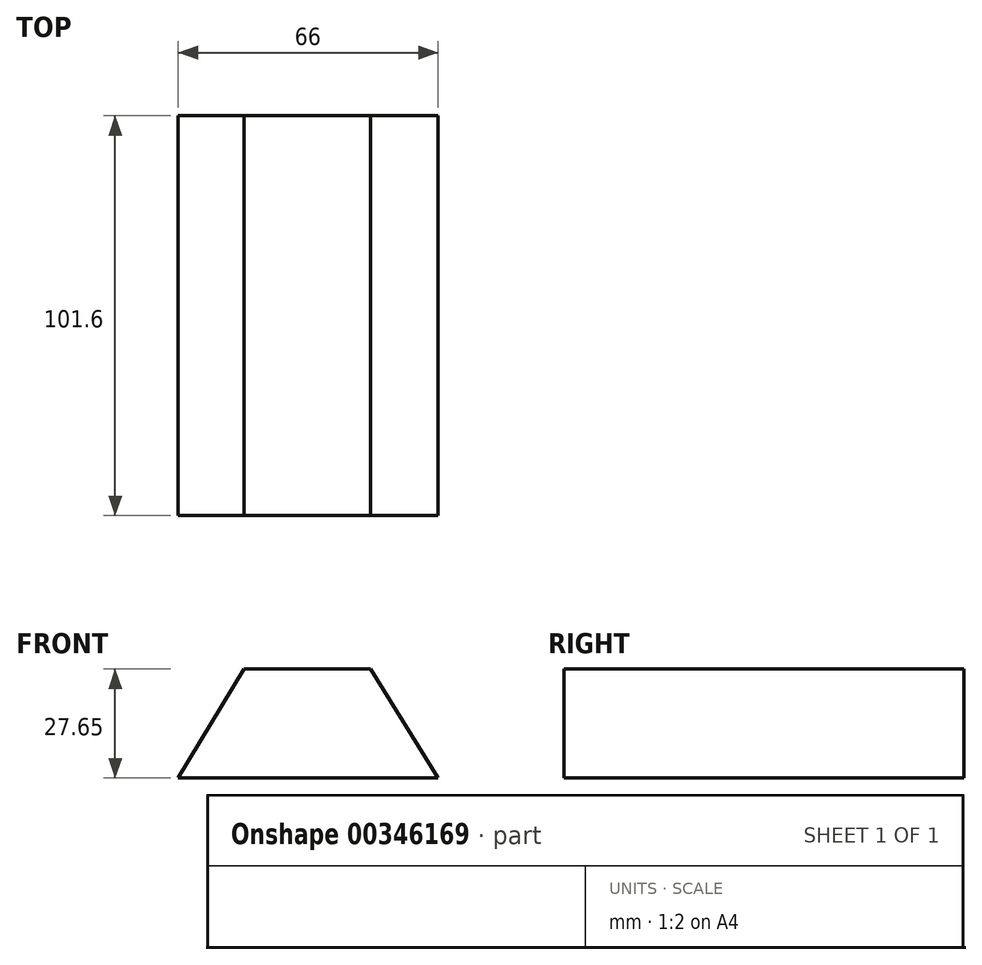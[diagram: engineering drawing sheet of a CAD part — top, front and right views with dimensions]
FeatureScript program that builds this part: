
annotation { "Feature Type Name" : "Feature", "Feature Type Description" : "" }
export const myFeature = defineFeature(function(context is Context, id is Id, definition is map)
    precondition{}
    {
        {
            var Q0;
            Q0=qCreatedBy(makeId("Front.planeOp"),FACE);
            var sketch = newSketch(context, id + "F0", { "sketchPlane" : qUnion([Q0])});
            skLineSegment(sketch, "E0", {"start": v(0, 0) * mm, "end": v(16.78, 27.65) * mm});
            skLineSegment(sketch, "E1", {"start": v(16.78, 27.65) * mm, "end": v(48.85, 27.65) * mm});
            skLineSegment(sketch, "E2", {"start": v(48.85, 27.65) * mm, "end": v(66, 0) * mm});
            skLineSegment(sketch, "E3", {"start": v(66, 0) * mm, "end": v(0, 0) * mm});
            skSolve(sketch);
        }
        {
            var Q0;
            Q0 = qSketchRegion(id + "F0", true);
            extrude(context, id + "F1", {"entities" : qUnion([Q0]), "depth" : 101.6 * mm});
        }
    });
